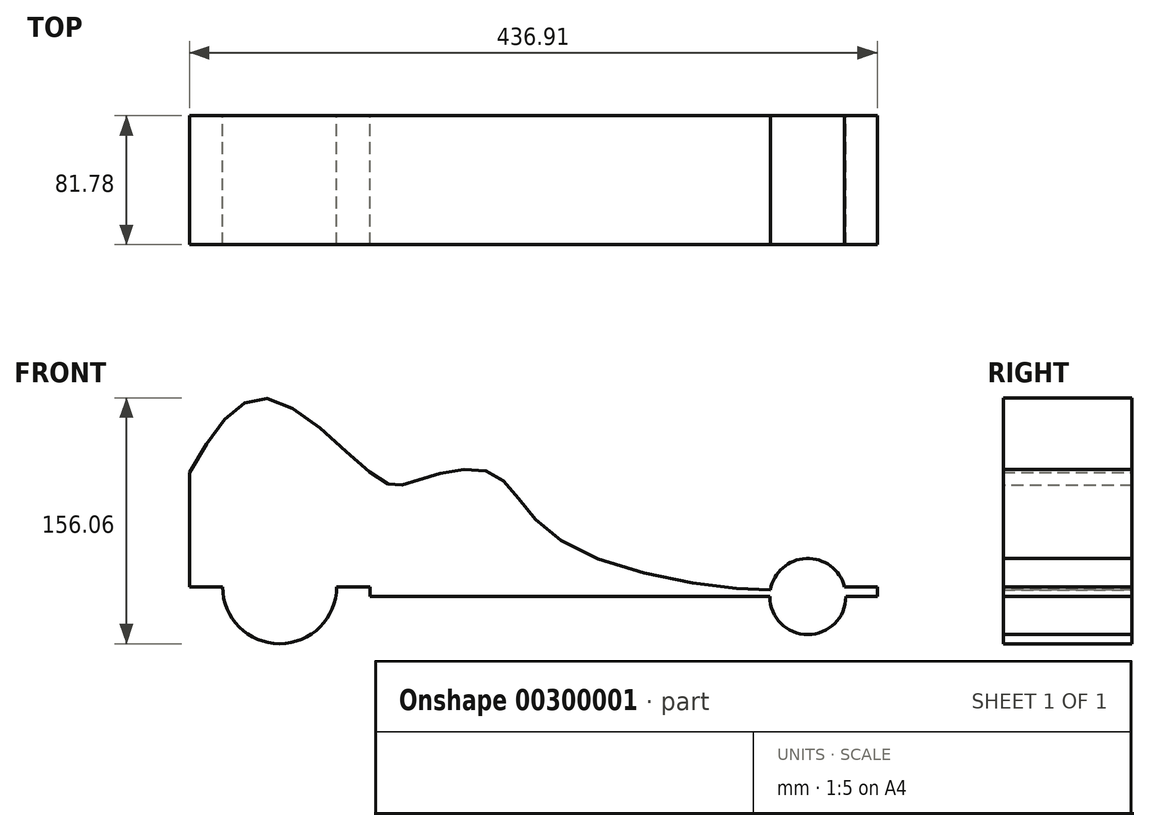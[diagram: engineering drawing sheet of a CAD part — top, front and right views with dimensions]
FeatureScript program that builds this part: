
annotation { "Feature Type Name" : "Feature", "Feature Type Description" : "" }
export const myFeature = defineFeature(function(context is Context, id is Id, definition is map)
    precondition{}
    {
        {
            var Q0;
            Q0=qCreatedBy(makeId("Front.planeOp"),FACE);
            var sketch = newSketch(context, id + "F0", { "sketchPlane" : qUnion([Q0])});
            skLineSegment(sketch, "E0", {"start": v(0, 0) * mm, "end": v(-76.68, 0) * mm});
            skLineSegment(sketch, "E1", {"start": v(-76.68, 0) * mm, "end": v(-76.68, 6.24) * mm});
            skLineSegment(sketch, "E2", {"start": v(-76.68, 6.24) * mm, "end": v(-191.26, 6.24) * mm});
            skLineSegment(sketch, "E3", {"start": v(0, 0) * mm, "end": v(188.14, 0) * mm});
            skLineSegment(sketch, "E4", {"start": v(188.14, 0) * mm, "end": v(214.89, 0) * mm});
            skLineSegment(sketch, "E5", {"start": v(214.89, 0) * mm, "end": v(245.65, 0) * mm});
            skLineSegment(sketch, "E6", {"start": v(245.65, 0) * mm, "end": v(245.65, 6.24) * mm});
            skLineSegment(sketch, "E7", {"start": v(245.65, 6.24) * mm, "end": v(214.89, 6.24) * mm});
            skFitSpline(sketch, "E8", {"points": [v(214.89, 6.24) * mm, v(202.95, 13) * mm, v(188.38, 6.24) * mm, v(187.93, 6.24) * mm], "startDerivative": vector(-23.22, 24.87) * mm, "endDerivative": vector(-3.57, 1.77) * mm});
            skLineSegment(sketch, "E9", {"start": v(-191.26, 6.24) * mm, "end": v(-191.26, 78.74) * mm});
            skFitSpline(sketch, "E10", {"points": [v(-191.26, 78.74) * mm, v(-141.7, 125.9) * mm, v(-69.48, 73.73) * mm, v(-47.13, 73.64) * mm, v(0, 78.74) * mm, v(48.56, 33.22) * mm, v(188.38, 6.24) * mm, v(122.77, 37.58) * mm], "startDerivative": vector(304.05, 523.37) * mm, "endDerivative": vector(-730.25, 270.52) * mm});
            skCircle(sketch, "E11", {"center": v(-133.97, 6.24) * mm, "radius": 36.21 * mm});
            skCircle(sketch, "E12", {"center": v(201.51, 0) * mm, "radius": 24.18 * mm});
            skSolve(sketch);
        }
        {
            var Q0;
            Q0 = qSketchRegion(id + "F0", true);
            extrude(context, id + "F1", {"entities" : qUnion([Q0]), "endBound" : BoundingType.SYMMETRIC, "depth" : 81.8 * mm});
        }
    });
